# Revit family: DFM Doors - zweiflügelige Türen OS 60
name_source: partatom
category: Doors
revit_build: Autodesk Revit 2017 (Build: 20190507_1515(x64)
units: mm (PartAtom-declared; Revit-internal decimal feet)

## family parameters
Always vertical = Yes
Cut with Voids When Loaded = No
Host = Wall
OmniClass Number = 23.30.10.00
OmniClass Title = Doors
Room Calculation Point = Yes
Shared = No

## types (1)
- 2500x2278.5 Innenzarge
    Autor = www.archispace.pl
    Breite zwischen den Zargen = 2329 mm  [stored 7.64108 ft]
    Eckzarge = No
    Fire Rating = EI 60
    Function = Interior
    Gangflügelsbreite = 1202 mm  [stored 3.94357 ft]
    Height = 2588 mm  [stored 8.49081 ft]
    Innenzarge = Yes
    Manufacturer = DFM Doors sp. z o. o.
    Material des Anschlagprofils = DFM Doors - aluminium
    Material für Lüftungsgitterverschnitt KWZ = DFM Doors - Lüftungsgitterverschnitt 1
    Material für Lüftungsgitterverschnitt NV und ZET = DFM Doors - Lüftungsgitterverschnitt 2
    Material für Wetterschutzschenkel = DFM Doors - verzinktes Stahlblech
    Material für das Lüftungsgitter = DFM Doors - verzinktes Stahlblech
    Material für den Beschlag = DFM Doors - aluminium
    Material für den Türflügel = DFM Doors - verzinktes Stahlblech
    Material für den Türschließer = DFM Doors - aluminium
    Material für die Türbänder = DFM Doors - Edelstahl
    Material für die Verglasung = DFM Doors - Verglasung
    Material für die Verglasungsrahmen = DFM Doors - verzinktes Stahlblech
    Material für die Zarge = DFM Doors - verzinktes Stahlblech
    Model = DFM OS 60 - 2
    Rough Height = 2588 mm  [stored 8.49081 ft]
    Rough Width = 2505 mm  [stored 8.2185 ft]
    Standflügelbreite = 1202 mm  [stored 3.94357 ft]
    Thickness = 65 mm  [stored 0.213255 ft]
    Türflügelhöhe = 2532 mm  [stored 8.30709 ft]
    URL = https://www.dfm-europe.eu
    Versatz der Gangflügelachse = 648 mm
    Versatz der Standflügelachse = 648 mm
    Versatz der Zwischenflügelachse = 1252.5 mm  [stored 4.10925 ft]
    Versatz des Türflügels = 47 mm  [stored 0.154199 ft]
    Wall Closure = By host
    Wandumfassungszarge = No
    Width = 2505 mm  [stored 8.2185 ft]
    Zarge typ = 2
    lichte Durchgangsbreite = 2278.5 mm  [stored 7.47539 ft]
    lichte Durchgangsbreite Max./Min. = ok
    lichte Durchgangsbreite bei geöffnetem Gangflügel = 1112 mm  [stored 3.64829 ft]
    lichte Durchgangshöhe = 2500 mm  [stored 8.2021 ft]
    lichte Durchgangshöhe Max./Min. = ok

note: [stored X ft] marks values corroborated as IEEE doubles in the binary element streams (Revit-internal decimal feet)
